# Revit family: OPTIMA_Compact_FLANGE_PN16_DN065-HF_RFA_2019
name_source: partatom
category: Pipe Accessories
units: mm (PartAtom-declared; Revit-internal decimal feet)

## family parameters
Always vertical = Yes
Cut with Voids When Loaded = No
Part Type = Valve - Breaks Into
Round Connector Dimension = Use Diameter
Shared = No
Work Plane-Based = No

## types (14) — shared parameters
CAT0 = Yes
Description = Tlakově nezávislý 2-cestný regulační vyvažovací ventil (PICV)
L2D_Min = 3048 mm
Manufacturer = Hydronix
QmdConnectorList = 301;D;302;D
URL = www.hydronix.cz
magiPartTypeId = 304

## per-type parameters (varying)
| type | D | DF2 | H1 | H2 | H3 | H4 | H6 | L2 | L2D | L3 | L4 | LF | LF2 | LF__ve | MC Product Code | R1 | R3 | R4 | Type Comments | W2D | magiProductFamilyId | magiProductId |
| Optima Compact Flange PN16 DN050 LF | 50 mm | 83 mm | 124 mm | 62 mm | 21 mm | 25 mm  [stored 0.082021 ft] | 157 mm | 115 mm | 230 mm | 193 mm | 108 mm | 18 mm | 9 mm  [stored 0.0295276 ft] | -18 mm | 53-1200 (DN50 LF; 20mm; pohon min 1000N; Qmin-dpmin 2500l/h-6.5kPa; Qmax-dpmin 15000l/h-20.0kPa; dpmax 800kPa) | 58 mm | 43 mm | 40 mm  [stored 0.131234 ft] | Přírubový; PN16; 0~120°C, s měřením | 50 mm  [stored 0.164042 ft] | Frese Optima Flange * | Frese Optima Flange DN050 LF |
| Optima Compact Flange PN16 DN050 HF | 50 mm | 83 mm | 124 mm | 62 mm | 21 mm | 25 mm  [stored 0.082021 ft] | 157 mm | 115 mm | 230 mm | 193 mm | 108 mm | 18 mm | 9 mm  [stored 0.0295276 ft] | -18 mm | 53-1210 (DN50 HF; 20mm; pohon min 1000N; Qmin-dpmin 3900l/h-19.0kPa; Qmax-dpmin 24000l/h-50.0kPa; dpmax 800kPa) | 58 mm | 43 mm | 40 mm  [stored 0.131234 ft] | Přírubový; PN16; 0~120°C, s měřením | 50 mm  [stored 0.164042 ft] | Frese Optima Flange * | Frese Optima Flange DN050 HF |
| Optima Compact Flange PN16 DN065 LF | 65 mm | 93 mm | 139 mm | 69 mm | 23 mm | 28 mm  [stored 0.0918635 ft] | 171 mm | 145 mm | 230 mm | 244 mm | 136 mm | 23 mm | 12 mm  [stored 0.0393701 ft] | -23 mm | 53-1201 (DN65 LF; 20mm; pohon min 1000N; Qmin-dpmin 4400l/h-15.0kPa; Qmax-dpmin 25000l/h-25.0kPa; dpmax 800kPa) | 73 mm | 48 mm  [stored 0.15748 ft] | 51 mm | Přírubový; PN16; 0~120°C, s měřením | 50 mm  [stored 0.164042 ft] | Frese Optima Flange * | Frese Optima Flange DN065 LF |
| Optima Compact Flange PN16 DN065 HF | 65 mm | 93 mm | 139 mm | 69 mm | 23 mm | 28 mm  [stored 0.0918635 ft] | 171 mm | 145 mm | 230 mm | 244 mm | 136 mm | 23 mm | 12 mm  [stored 0.0393701 ft] | -23 mm | 53-1211 (DN65 HF; 20mm; pohon min 1000N; Qmin-dpmin 6000l/h-30.0kPa; Qmax-dpmin 35000l/h-55.0kPa; dpmax 800kPa) | 73 mm | 48 mm  [stored 0.15748 ft] | 51 mm | Přírubový; PN16; 0~120°C, s měřením | 50 mm  [stored 0.164042 ft] | Frese Optima Flange * | Frese Optima Flange DN065 HF |
| Optima Compact Flange PN16 DN080 LF | 80 mm | 100 mm | 150 mm | 75 mm | 25 mm  [stored 0.082021 ft] | 30 mm  [stored 0.0984252 ft] | 183 mm | 155 mm | 230 mm | 260 mm | 146 mm | 25 mm  [stored 0.082021 ft] | 12 mm  [stored 0.0393701 ft] | -25 mm | 53-1202 (DN80 LF; 20mm; pohon min 1000N; Qmin-dpmin 5300l/h-16.0kPa; Qmax-dpmin 34000l/h-25.0kPa; dpmax 800kPa) | 78 mm | 52 mm  [stored 0.170604 ft] | 54 mm | Přírubový; PN16; 0~120°C, s měřením | 50 mm  [stored 0.164042 ft] | Frese Optima Flange * | Frese Optima Flange DN080 LF |
| Optima Compact Flange PN16 DN080 HF | 80 mm | 100 mm | 150 mm | 75 mm | 25 mm  [stored 0.082021 ft] | 30 mm  [stored 0.0984252 ft] | 183 mm | 155 mm | 230 mm | 260 mm | 146 mm | 25 mm  [stored 0.082021 ft] | 12 mm  [stored 0.0393701 ft] | -25 mm | 53-1212 (DN80 HF; 20mm; pohon min 1000N; Qmin-dpmin 7000l/h-23.0kPa; Qmax-dpmin 43000l/h-50.0kPa; dpmax 800kPa) | 78 mm | 52 mm  [stored 0.170604 ft] | 54 mm | Přírubový; PN16; 0~120°C, s měřením | 50 mm  [stored 0.164042 ft] | Frese Optima Flange * | Frese Optima Flange DN080 HF |
| Optima Compact Flange PN16 DN100 LF | 100 mm | 118 mm | 176 mm | 88 mm | 29 mm | 35 mm | 269 mm | 175 mm | 230 mm | 294 mm | 165 mm | 28 mm  [stored 0.0918635 ft] | 14 mm  [stored 0.0459318 ft] | -28 mm  [stored -0.0918635 ft] | 53-1203 (DN100 LF; 40mm; pohon min 1000N; Qmin-dpmin 12100l/h-20.0kPa; Qmax-dpmin 68000l/h-35.0kPa; dpmax 800kPa) | 88 mm | 61 mm | 61 mm | Přírubový; PN16; 0~120°C, s měřením | 50 mm  [stored 0.164042 ft] | Frese Optima Flange * | Frese Optima Flange DN100 LF |
| Optima Compact Flange PN16 DN100 HF | 100 mm | 118 mm | 176 mm | 88 mm | 29 mm | 35 mm | 269 mm | 175 mm | 230 mm | 294 mm | 165 mm | 28 mm  [stored 0.0918635 ft] | 14 mm  [stored 0.0459318 ft] | -28 mm  [stored -0.0918635 ft] | 53-1213 (DN100 HF; 40mm; pohon min 1000N; Qmin-dpmin 14800l/h-30.0kPa; Qmax-dpmin 90000l/h-75.0kPa; dpmax 800kPa) | 88 mm | 61 mm | 61 mm | Přírubový; PN16; 0~120°C, s měřením | 50 mm  [stored 0.164042 ft] | Frese Optima Flange * | Frese Optima Flange DN100 HF |
| Optima Compact Flange PN16 DN125 LF | 125 mm | 135 mm | 203 mm | 101 mm | 34 mm | 41 mm | 276 mm | 200 mm | 230 mm | 336 mm | 188 mm | 32 mm  [stored 0.104987 ft] | 16 mm  [stored 0.0524934 ft] | -32 mm  [stored -0.104987 ft] | 53-1204 (DN125 LF; 40mm; pohon min 1000N; Qmin-dpmin 18500l/h-16.0kPa; Qmax-dpmin 110000l/h-35.0kPa; dpmax 800kPa) | 100 mm | 70 mm  [stored 0.229659 ft] | 70 mm  [stored 0.229659 ft] | Přírubový; PN16; 0~120°C, s měřením | 50 mm  [stored 0.164042 ft] | Frese Optima Flange * | Frese Optima Flange DN125 LF |
| Optima Compact Flange PN16 DN125 HF | 125 mm | 135 mm | 203 mm | 101 mm | 34 mm | 41 mm | 276 mm | 200 mm | 230 mm | 336 mm | 188 mm | 32 mm  [stored 0.104987 ft] | 16 mm  [stored 0.0524934 ft] | -32 mm  [stored -0.104987 ft] | 53-1214 (DN125 HF; 40mm; pohon min 1000N; Qmin-dpmin 23000l/h-27.0kPa; Qmax-dpmin 135000l/h-53.0kPa; dpmax 800kPa) | 100 mm | 70 mm  [stored 0.229659 ft] | 70 mm  [stored 0.229659 ft] | Přírubový; PN16; 0~120°C, s měřením | 50 mm  [stored 0.164042 ft] | Frese Optima Flange * | Frese Optima Flange DN125 HF |
| Optima Compact Flange PN16 DN150 LF | 150 mm | 143 mm | 214 mm | 107 mm | 36 mm | 43 mm | 279 mm | 240 mm | 230 mm | 403 mm | 226 mm | 38 mm | 19 mm | -38 mm | 53-1205 (DN150 LF; 43mm; pohon min 1500N; Qmin-dpmin 25600l/h-21.0kPa; Qmax-dpmin 148000l/h-35.0kPa; dpmax 800kPa) | 120 mm | 74 mm | 84 mm | Přírubový; PN16; 0~110°C, s měřením | 50 mm  [stored 0.164042 ft] | Frese Optima Flange * | Frese Optima Flange DN150 LF |
| Optima Compact Flange PN16 DN150 HF | 150 mm | 143 mm | 214 mm | 107 mm | 36 mm | 43 mm | 279 mm | 240 mm | 230 mm | 403 mm | 226 mm | 38 mm | 19 mm | -38 mm | 53-1215 (DN150 HF; 43mm; pohon min 1500N; Qmin-dpmin 32000l/h-33.0kPa; Qmax-dpmin 195000l/h-65.0kPa; dpmax 800kPa) | 120 mm | 74 mm | 84 mm | Přírubový; PN16; 0~110°C, s měřením | 50 mm  [stored 0.164042 ft] | Frese Optima Flange * | Frese Optima Flange DN150 HF |
| Optima Compact Flange PN16 DN200 LF | 200 mm | 190 mm | 380 mm | 209 mm | 15 mm  [stored 0.0492126 ft] | 57 mm  [stored 0.187008 ft] | 281 mm | 300 mm | 350 mm | 504 mm | 282 mm | 48 mm  [stored 0.15748 ft] | 24 mm  [stored 0.0787402 ft] | -48 mm  [stored -0.15748 ft] | 53-1206 (DN200 LF; 43mm; pohon min 1500N; Qmin-dpmin 95000l/h-11.0kPa; Qmax-dpmin 210000l/h-32.0kPa; dpmax 800kPa) | 235 mm | 99 mm | 165 mm | Přírubový; PN16; 0~110°C, s měřením | 100 mm |  |  |
| Optima Compact Flange PN16 DN200 HF | 200 mm | 190 mm | 380 mm | 209 mm | 15 mm  [stored 0.0492126 ft] | 57 mm  [stored 0.187008 ft] | 281 mm | 300 mm | 350 mm | 504 mm | 282 mm | 48 mm  [stored 0.15748 ft] | 24 mm  [stored 0.0787402 ft] | -48 mm  [stored -0.15748 ft] | 53-1216 (DN200 HF; 43mm; pohon min 1500N; Qmin-dpmin 130000l/h-31.0kPa; Qmax-dpmin 280000l/h-78.0kPa; dpmax 800kPa) | 235 mm | 99 mm | 165 mm | Přírubový; PN16; 0~110°C, s měřením | 100 mm |  |  |

note: [stored X ft] marks values corroborated as IEEE doubles in the binary element streams (Revit-internal decimal feet)

## geometry (parser evidence)
native form markers: Sweep x1
no freeform markers — native parametric forms only
